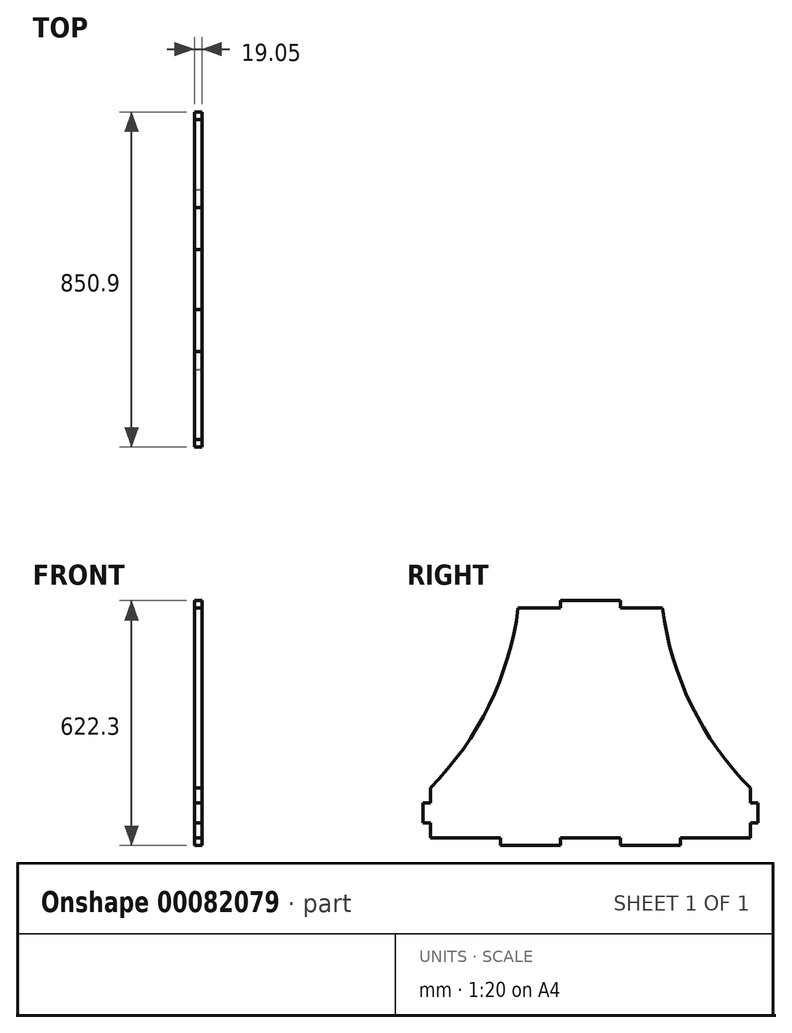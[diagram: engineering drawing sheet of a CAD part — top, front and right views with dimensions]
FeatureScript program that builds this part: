
annotation { "Feature Type Name" : "Feature", "Feature Type Description" : "" }
export const myFeature = defineFeature(function(context is Context, id is Id, definition is map)
    precondition{}
    {
        {
            var Q0;
            Q0=qCreatedBy(makeId("Right.planeOp"),FACE);
            var sketch = newSketch(context, id + "F0", { "sketchPlane" : qUnion([Q0])});
            skLineSegment(sketch, "E0", {"start": v(-208.02, -101.37) * mm, "end": v(-208.02, 25.63) * mm});
            skLineSegment(sketch, "E1", {"start": v(-208.02, -101.37) * mm, "end": v(604.78, -101.37) * mm});
            skLineSegment(sketch, "E2", {"start": v(604.78, -101.37) * mm, "end": v(604.78, 25.63) * mm});
            skLineSegment(sketch, "E3", {"start": v(198.38, 609.83) * mm, "end": v(20.58, 609.83) * mm});
            skLineSegment(sketch, "E4", {"start": v(198.38, 609.83) * mm, "end": v(376.18, 609.83) * mm});
            skArc(sketch, "E5", {"start": v(-208.02, 25.63) * mm, "mid": v(-33.03, 293.98) * mm, "end": v(20.58, 609.83) * mm});
            skArc(sketch, "E6", {"start": v(376.18, 609.83) * mm, "mid": v(429.79, 293.98) * mm, "end": v(604.78, 25.63) * mm});
            skPoint(sketch, "E7.start.orphan", {"position": v(198.38, -101.37) * mm});
            skLineSegment(sketch, "E8.0", {"start": v(198.38, 482.83) * mm, "end": v(20.58, 482.83) * mm});
            skLineSegment(sketch, "E8.1", {"start": v(198.38, 482.83) * mm, "end": v(376.18, 482.83) * mm});
            skSolve(sketch);
        }
        {
            var Q0;
            Q0 = qSketchRegion(id + "F0", true);
            extrude(context, id + "F1", {"entities" : qUnion([Q0]), "depth" : 19.05 * mm});
        }
        {
            var Q0;
            Q0=makeQuery(id+"F1.opExtrude","CAP_FACE",FACE,{"disambiguationData":[OSD([sQuery(id+"F0.wireOp",EDGE,"E0"),sQuery(id+"F0.wireOp",EDGE,"E1"),sQuery(id+"F0.wireOp",EDGE,"E2"),sQuery(id+"F0.wireOp",EDGE,"E3"),sQuery(id+"F0.wireOp",EDGE,"E4"),sQuery(id+"F0.wireOp",EDGE,"E5"),sQuery(id+"F0.wireOp",EDGE,"E6")])],"isStart":false});
            var sketch = newSketch(context, id + "F2", { "sketchPlane" : qUnion([Q0])});
            skLineSegment(sketch, "E9", {"start": v(198.38, 628.88) * mm, "end": v(122.18, 628.88) * mm});
            skLineSegment(sketch, "E10", {"start": v(198.38, 628.88) * mm, "end": v(274.58, 628.88) * mm});
            skLineSegment(sketch, "E11.bottom", {"start": v(122.18, 628.88) * mm, "end": v(274.58, 628.88) * mm});
            skLineSegment(sketch, "E11.top", {"start": v(122.18, 609.83) * mm, "end": v(274.58, 609.83) * mm});
            skLineSegment(sketch, "E11.left", {"start": v(122.18, 628.88) * mm, "end": v(122.18, 609.83) * mm});
            skLineSegment(sketch, "E11.right", {"start": v(274.58, 628.88) * mm, "end": v(274.58, 609.83) * mm});
            skPoint(sketch, "E12.start.orphan", {"position": v(198.38, 609.83) * mm});
            skLineSegment(sketch, "E13", {"start": v(-227.07, -37.87) * mm, "end": v(-227.07, -12.47) * mm});
            skLineSegment(sketch, "E14", {"start": v(-227.07, -37.87) * mm, "end": v(-227.07, -63.27) * mm});
            skPoint(sketch, "E15.start.orphan", {"position": v(-208.02, -37.87) * mm});
            skLineSegment(sketch, "E16.bottom", {"start": v(-227.07, -12.47) * mm, "end": v(-208.02, -12.47) * mm});
            skLineSegment(sketch, "E16.top", {"start": v(-227.07, -63.27) * mm, "end": v(-208.02, -63.27) * mm});
            skLineSegment(sketch, "E16.left", {"start": v(-227.07, -12.47) * mm, "end": v(-227.07, -63.27) * mm});
            skLineSegment(sketch, "E16.right", {"start": v(-208.02, -12.47) * mm, "end": v(-208.02, -63.27) * mm});
            skLineSegment(sketch, "E17", {"start": v(-208.02, -101.37) * mm, "end": v(-30.22, -101.37) * mm});
            skLineSegment(sketch, "E18", {"start": v(-30.22, -101.37) * mm, "end": v(122.18, -101.37) * mm});
            skLineSegment(sketch, "E19.top", {"start": v(-30.22, -120.42) * mm, "end": v(122.18, -120.42) * mm});
            skLineSegment(sketch, "E19.left", {"start": v(-30.22, -101.37) * mm, "end": v(-30.22, -120.42) * mm});
            skLineSegment(sketch, "E19.right", {"start": v(122.18, -101.37) * mm, "end": v(122.18, -120.42) * mm});
            skLineSegment(sketch, "E20", {"start": v(198.38, -101.37) * mm, "end": v(198.38, 37.9) * mm});
            skLineSegment(sketch, "E21.MirrorCS", {"start": v(426.98, -101.37) * mm, "end": v(426.98, -120.42) * mm});
            skLineSegment(sketch, "E22.MirrorCS", {"start": v(274.58, -101.37) * mm, "end": v(274.58, -120.42) * mm});
            skLineSegment(sketch, "E23.MirrorCS", {"start": v(426.98, -101.37) * mm, "end": v(274.58, -101.37) * mm});
            skLineSegment(sketch, "E24.MirrorCS", {"start": v(426.98, -120.42) * mm, "end": v(274.58, -120.42) * mm});
            skLineSegment(sketch, "E25.MirrorCS", {"start": v(604.78, -101.37) * mm, "end": v(426.98, -101.37) * mm});
            skLineSegment(sketch, "E26.MirrorCS", {"start": v(623.83, -37.87) * mm, "end": v(623.83, -12.47) * mm});
            skLineSegment(sketch, "E27.MirrorCS", {"start": v(623.83, -37.87) * mm, "end": v(623.83, -63.27) * mm});
            skLineSegment(sketch, "E28.MirrorCS", {"start": v(623.83, -63.27) * mm, "end": v(604.78, -63.27) * mm});
            skLineSegment(sketch, "E29.MirrorCS", {"start": v(604.78, -12.47) * mm, "end": v(604.78, -63.27) * mm});
            skLineSegment(sketch, "E30.MirrorCS", {"start": v(623.83, -12.47) * mm, "end": v(623.83, -63.27) * mm});
            skLineSegment(sketch, "E31.MirrorCS", {"start": v(623.83, -12.47) * mm, "end": v(604.78, -12.47) * mm});
            skPoint(sketch, "E32.MirrorP", {"position": v(604.78, -37.87) * mm});
            skSolve(sketch);
        }
        {
            var Q0;
            Q0 = qSketchRegion(id + "F2", true);
            extrude(context, id + "F3", {"entities" : qUnion([Q0]), "operationType" : NewBodyOperationType.ADD, "oppositeDirection" : true, "depth" : 19.05 * mm});
        }
        {
            var Q0;
            Q0 = qSketchRegion(id + "F0", true);
            extrude(context, id + "F4", {"entities" : qUnion([Q0]), "operationType" : NewBodyOperationType.ADD, "depth" : 19.05 * mm});
        }
        {
            var Q0;
            Q0=makeQuery(id+"F3.boolean.opBoolean","MERGE",FACE,{"derivedFrom":[makeQuery(id+"F1.opExtrude","CAP_FACE",FACE,{"disambiguationData":[OSD([sQuery(id+"F0.wireOp",EDGE,"E0"),sQuery(id+"F0.wireOp",EDGE,"E1"),sQuery(id+"F0.wireOp",EDGE,"E2"),sQuery(id+"F0.wireOp",EDGE,"E3"),sQuery(id+"F0.wireOp",EDGE,"E4"),sQuery(id+"F0.wireOp",EDGE,"E5"),sQuery(id+"F0.wireOp",EDGE,"E6")])],"isStart":false}),makeQuery(id+"F3.opExtrude","CAP_FACE",FACE,{"disambiguationData":[OSD([sQuery(id+"F2.wireOp",EDGE,"E11.bottom"),sQuery(id+"F2.wireOp",EDGE,"E11.top"),sQuery(id+"F2.wireOp",EDGE,"E11.left"),sQuery(id+"F2.wireOp",EDGE,"E11.right")])],"isStart":true}),makeQuery(id+"F3.opExtrude","CAP_FACE",FACE,{"disambiguationData":[OSD([sQuery(id+"F2.wireOp",EDGE,"E16.bottom"),sQuery(id+"F2.wireOp",EDGE,"E16.top"),sQuery(id+"F2.wireOp",EDGE,"E16.left"),sQuery(id+"F2.wireOp",EDGE,"E16.right")])],"isStart":true}),makeQuery(id+"F3.opExtrude","CAP_FACE",FACE,{"disambiguationData":[OSD([sQuery(id+"F2.wireOp",EDGE,"E18"),sQuery(id+"F2.wireOp",EDGE,"E19.top"),sQuery(id+"F2.wireOp",EDGE,"E19.left"),sQuery(id+"F2.wireOp",EDGE,"E19.right")])],"isStart":true}),makeQuery(id+"F3.opExtrude","CAP_FACE",FACE,{"disambiguationData":[OSD([sQuery(id+"F2.wireOp",EDGE,"E21.MirrorCS"),sQuery(id+"F2.wireOp",EDGE,"E22.MirrorCS"),sQuery(id+"F2.wireOp",EDGE,"E23.MirrorCS"),sQuery(id+"F2.wireOp",EDGE,"E24.MirrorCS")])],"isStart":true}),makeQuery(id+"F3.opExtrude","CAP_FACE",FACE,{"disambiguationData":[OSD([sQuery(id+"F2.wireOp",EDGE,"E28.MirrorCS"),sQuery(id+"F2.wireOp",EDGE,"E29.MirrorCS"),sQuery(id+"F2.wireOp",EDGE,"E30.MirrorCS"),sQuery(id+"F2.wireOp",EDGE,"E31.MirrorCS")])],"isStart":true})]});
            var sketch = newSketch(context, id + "F5", { "sketchPlane" : qUnion([Q0])});
            skLineSegment(sketch, "E33.0", {"start": v(14.98, 482.83) * mm, "end": v(122.18, 482.83) * mm});
            skLineSegment(sketch, "E34.0", {"start": v(274.58, 482.83) * mm, "end": v(381.78, 482.83) * mm});
            skLineSegment(sketch, "E35.0", {"start": v(122.18, 501.88) * mm, "end": v(274.58, 501.88) * mm});
            skLineSegment(sketch, "E36", {"start": v(122.18, 501.88) * mm, "end": v(122.18, 482.83) * mm});
            skLineSegment(sketch, "E37", {"start": v(274.58, 501.88) * mm, "end": v(274.58, 482.83) * mm});
            skLineSegment(sketch, "E38", {"start": v(20.58, 609.83) * mm, "end": v(122.18, 609.83) * mm});
            skLineSegment(sketch, "E39", {"start": v(122.18, 609.83) * mm, "end": v(122.18, 628.88) * mm});
            skLineSegment(sketch, "E40", {"start": v(122.18, 628.88) * mm, "end": v(274.58, 628.88) * mm});
            skLineSegment(sketch, "E41", {"start": v(274.58, 628.88) * mm, "end": v(274.58, 609.83) * mm});
            skLineSegment(sketch, "E42", {"start": v(274.58, 609.83) * mm, "end": v(376.18, 609.83) * mm});
            skArc(sketch, "E43", {"start": v(14.98, 482.83) * mm, "mid": v(20.34, 546.21) * mm, "end": v(20.58, 609.83) * mm});
            skArc(sketch, "E44", {"start": v(376.18, 609.83) * mm, "mid": v(376.41, 546.21) * mm, "end": v(381.78, 482.83) * mm});
            skSolve(sketch);
        }
        {
            var Q0;
            Q0 = qSketchRegion(id + "F5", true);
            extrude(context, id + "F6", {"entities" : qUnion([Q0]), "operationType" : NewBodyOperationType.REMOVE, "endBound" : BoundingType.THROUGH_ALL, "oppositeDirection" : true, "depth" : 25.4 * mm});
        }
    });
